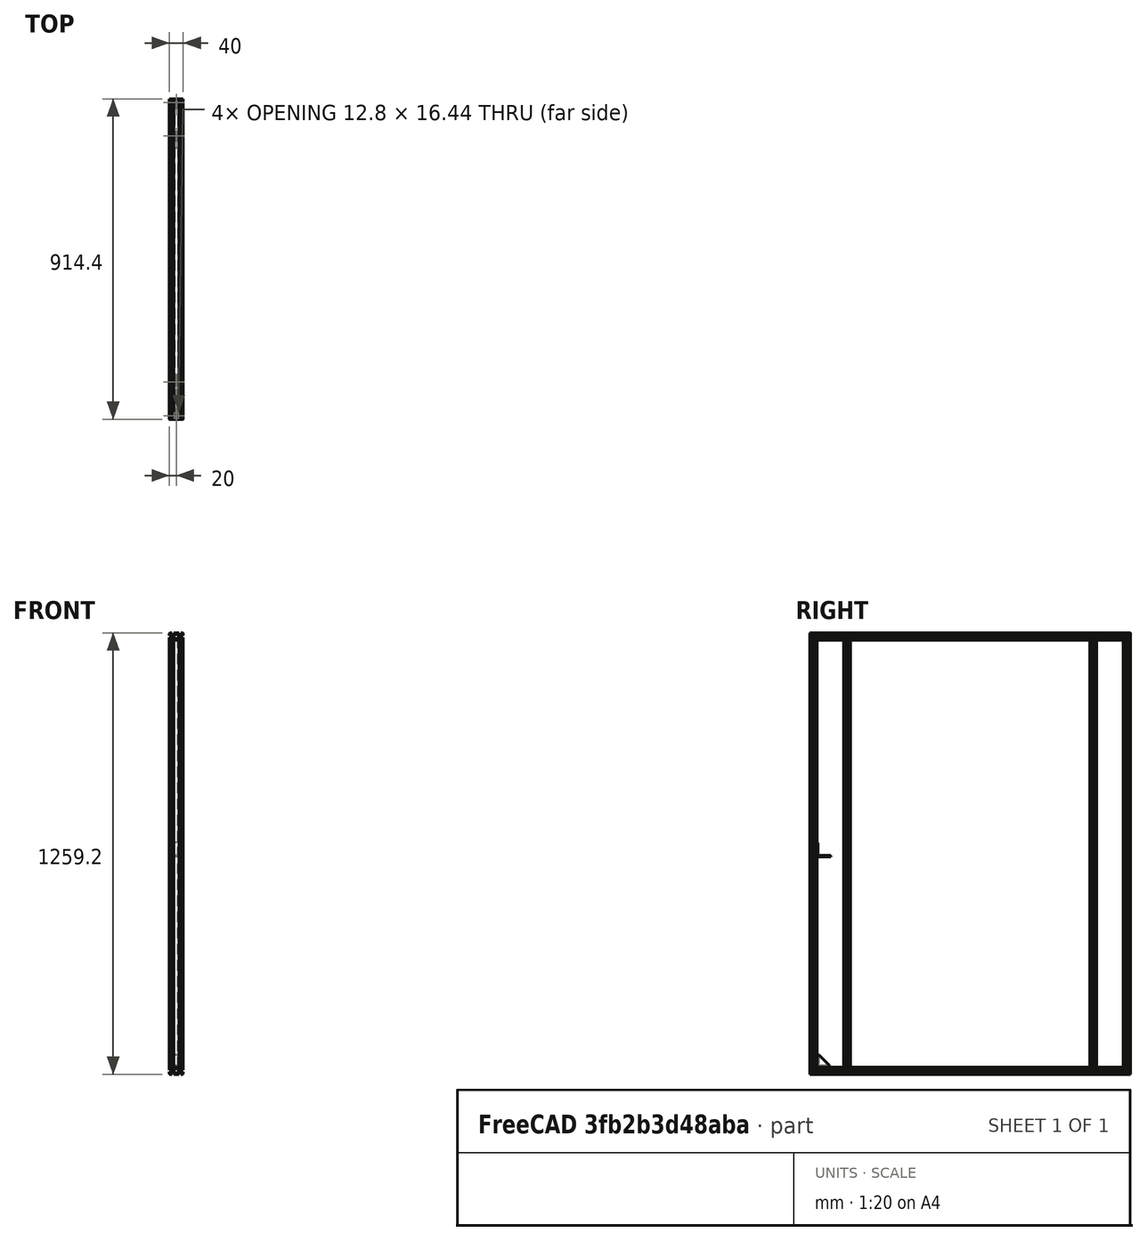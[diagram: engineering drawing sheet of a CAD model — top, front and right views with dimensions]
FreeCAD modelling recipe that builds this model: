
FCSTD DOCUMENT  (FreeCAD 0.19R)
Label: design
License: All rights reserved
LicenseURL: http://en.wikipedia.org/wiki/All_rights_reserved
objects: App::FeaturePython×54, Part::FeaturePython×34, Part::Feature×8
note: 41 computed .brp shape members not serialized (recipe doc carries the construction recipe); baked Part::Feature solids carry a one-line shape summary decoded from their .brp

FEATURE [Part::Feature] Part__Feature  label="Left Side Inner 5537T16_T-Slotted Framing"
  Placement = pos=(468.64,437.451,18.9991) rot=(0,0,1;0rad)
  shape: bbox 40 x 20 x 1219 mm, 102 faces (baked)
FEATURE [Part::Feature] Part__Feature001  label="Left Side Outer 5537T16_T-Slotted Framing"
  Placement = pos=(468.64,533.651,18.9991) rot=(0,0,1;0rad)
  shape: bbox 40 x 20 x 1219 mm, 102 faces (baked)
FEATURE [Part::Feature] Part__Feature002  label="Right Side Inner 5537T16_T-Slotted Framing"
  Placement = pos=(468.64,-264.549,18.9991) rot=(0,0,1;0rad)
  shape: bbox 40 x 20 x 1219 mm, 102 faces (baked)
FEATURE [Part::Feature] Part__Feature003  label="Right Side Outer 5537T16_T-Slotted Framing"
  Placement = pos=(468.64,-360.749,18.9991) rot=(0,0,1;0rad)
  shape: bbox 40 x 20 x 1219 mm, 102 faces (baked)
FEATURE [Part::Feature] Part__Feature004  label="Top Side 5537T706_T-Slotted Framing"
  Placement = pos=(468.64,86.451,638.599) rot=(1,0,0;1.5708rad)
  shape: bbox 40 x 914.4 x 20 mm, 102 faces (baked)
FEATURE [Part::Feature] Part__Feature005  label="Bottom Side 5537T706_T-Slotted Framing"
  Placement = pos=(468.64,86.451,-600.601) rot=(-1,0,0;4.71239rad)
  shape: bbox 40 x 914.4 x 20 mm, 102 faces (baked)
FEATURE [Part::Feature] Solid  label="5537T442_T-Slotted Framing"
  Placement = pos=(467.64,-350.749,10.5111) rot=(0.57735,0.57735,0.57735;2.0944rad)
  shape: bbox 38 x 40 x 40 mm, 25 faces (baked)
FEATURE [Part::Feature] Solid001  label="5537T197_T-Slotted Framing"
  Placement = pos=(467.64,-350.749,-590.601) rot=(0,-1,0;1.5708rad)
  shape: bbox 38 x 38 x 38 mm, 67 faces (baked)
FEATURE [Part::FeaturePython] Parts  # WARN: FeaturePython — macro-defined, semantics opaque (R4)
  Group = -> [Part__Feature004,Part__Feature,Part__Feature001,Part__Feature002,Part__Feature003,Part__Feature005,Solid,Solid001]
  GroupMode = 0
FEATURE [Part::FeaturePython] Assembly  # WARN: FeaturePython — macro-defined, semantics opaque (R4)
  AutoRelax = true
  BuildShape = 0
  Freeze = false
  Group = -> [Constraints,Elements,Parts]
  Verbose = false
  _SolverType = 1
  _Version = 1
FEATURE [App::FeaturePython] Constraints  # WARN: FeaturePython — macro-defined, semantics opaque (R4)
  Group = -> [Constraint,Constraint001,Constraint002,Constraint003,Constraint004,Constraint007,Constraint008,Constraint009,Constraint010,Constraint011,Constraint012,Constraint013,Constraint014,Constraint015,Constraint016,Constraint017]
  _Version = 1
FEATURE [App::FeaturePython] Elements  # WARN: FeaturePython — macro-defined, semantics opaque (R4)
  Group = -> [_Element,_Element001,_Element002,_Element003,_Element004,_Element005,_Element006,_Element007,_Element008,_Element009,_Element010,_Element011,_Element012,_Element013,_Element014,_Element015,_Element016,_Element017,_Element018,_Element019,_Element020,_Element021,_Element022,_Element023,_Element024,_Element025,_Element028,_Element029,_Element030,_Element031,_Element032,_Element033]
FEATURE [App::FeaturePython] Constraint  label="Side_End_Alignment"  # WARN: FeaturePython — macro-defined, semantics opaque (R4)
  Angle = 0
  AnglePitch = 0
  AngleRoll = 0
  Cascade = false
  Disabled = false
  Group = -> [ElementLink,ElementLink001,ElementLink002,ElementLink003]
  LockAngle = false
  _ConstraintType = 37
  _Parent = -> Constraints
FEATURE [App::FeaturePython] ElementLink  label="_Element"  # link proxy (typed FeaturePython)
  LinkTransform = true
  LinkedObject = -> _Element
  _Parent = -> Constraint
FEATURE [Part::FeaturePython] _Element  # link proxy (typed FeaturePython)
  Detach = false
  LinkTransform = true
  LinkedObject = -> Part__Feature003 [Face20]
  _Parent = -> Elements
FEATURE [App::FeaturePython] ElementLink001  label="_Element001"  # link proxy (typed FeaturePython)
  LinkTransform = true
  LinkedObject = -> _Element001
  _Parent = -> Constraint
FEATURE [Part::FeaturePython] _Element001  # link proxy (typed FeaturePython)
  Detach = false
  LinkTransform = true
  LinkedObject = -> Part__Feature002 [Face20]
  _Parent = -> Elements
FEATURE [App::FeaturePython] ElementLink002  label="_Element002"  # link proxy (typed FeaturePython)
  LinkTransform = true
  LinkedObject = -> _Element002
  _Parent = -> Constraint
FEATURE [Part::FeaturePython] _Element002  # link proxy (typed FeaturePython)
  Detach = false
  LinkTransform = true
  LinkedObject = -> Part__Feature [Face20]
  _Parent = -> Elements
FEATURE [App::FeaturePython] ElementLink003  label="_Element003"  # link proxy (typed FeaturePython)
  LinkTransform = true
  LinkedObject = -> _Element003
  _Parent = -> Constraint
FEATURE [Part::FeaturePython] _Element003  # link proxy (typed FeaturePython)
  Detach = false
  LinkTransform = true
  LinkedObject = -> Part__Feature001 [Face20]
  _Parent = -> Elements
FEATURE [App::FeaturePython] Constraint001  label="Side_Top_Alignment"  # WARN: FeaturePython — macro-defined, semantics opaque (R4)
  Angle = 0
  AnglePitch = 0
  AngleRoll = 0
  Cascade = false
  Disabled = false
  Group = -> [ElementLink004,ElementLink005,ElementLink006,ElementLink007]
  LockAngle = false
  _ConstraintType = 37
  _Parent = -> Constraints
FEATURE [App::FeaturePython] ElementLink004  label="_Element004"  # link proxy (typed FeaturePython)
  LinkTransform = true
  LinkedObject = -> _Element004
  _Parent = -> Constraint001
FEATURE [Part::FeaturePython] _Element004  # link proxy (typed FeaturePython)
  Detach = false
  LinkTransform = true
  LinkedObject = -> Part__Feature003 [Face28]
  _Parent = -> Elements
FEATURE [App::FeaturePython] ElementLink005  label="_Element005"  # link proxy (typed FeaturePython)
  LinkTransform = true
  LinkedObject = -> _Element005
  _Parent = -> Constraint001
FEATURE [Part::FeaturePython] _Element005  # link proxy (typed FeaturePython)
  Detach = false
  LinkTransform = true
  LinkedObject = -> Part__Feature002 [Face28]
  _Parent = -> Elements
FEATURE [App::FeaturePython] ElementLink006  label="_Element006"  # link proxy (typed FeaturePython)
  LinkTransform = true
  LinkedObject = -> _Element006
  _Parent = -> Constraint001
FEATURE [Part::FeaturePython] _Element006  # link proxy (typed FeaturePython)
  Detach = false
  LinkTransform = true
  LinkedObject = -> Part__Feature [Face28]
  _Parent = -> Elements
FEATURE [App::FeaturePython] ElementLink007  label="_Element007"  # link proxy (typed FeaturePython)
  LinkTransform = true
  LinkedObject = -> _Element007
  _Parent = -> Constraint001
FEATURE [Part::FeaturePython] _Element007  # link proxy (typed FeaturePython)
  Detach = false
  LinkTransform = true
  LinkedObject = -> Part__Feature001 [Face28]
  _Parent = -> Elements
FEATURE [Part::FeaturePython] _Element008  # link proxy (typed FeaturePython)
  Detach = false
  LinkTransform = true
  LinkedObject = -> Part__Feature004 [Face19]
  _Parent = -> Elements
FEATURE [Part::FeaturePython] _Element009  # link proxy (typed FeaturePython)
  Detach = false
  LinkTransform = true
  LinkedObject = -> Part__Feature005 [Face19]
  _Parent = -> Elements
FEATURE [Part::FeaturePython] _Element010  # link proxy (typed FeaturePython)
  Detach = false
  LinkTransform = true
  LinkedObject = -> Part__Feature005 [Face60]
  _Parent = -> Elements
FEATURE [Part::FeaturePython] _Element011  # link proxy (typed FeaturePython)
  Detach = false
  LinkTransform = true
  LinkedObject = -> Part__Feature004 [Face60]
  _Parent = -> Elements
FEATURE [App::FeaturePython] Constraint002  label="PlaneAlignment"  # WARN: FeaturePython — macro-defined, semantics opaque (R4)
  Angle = 0
  AnglePitch = 0
  AngleRoll = 0
  Cascade = false
  Disabled = false
  Group = -> [ElementLink008,ElementLink009]
  LockAngle = false
  _ConstraintType = 37
  _Parent = -> Constraints
FEATURE [App::FeaturePython] ElementLink008  label="_Element012"  # link proxy (typed FeaturePython)
  LinkTransform = true
  LinkedObject = -> _Element012
  _Parent = -> Constraint002
FEATURE [Part::FeaturePython] _Element012  # link proxy (typed FeaturePython)
  Detach = false
  LinkTransform = true
  LinkedObject = -> Part__Feature005 [Face55]
  _Parent = -> Elements
FEATURE [App::FeaturePython] ElementLink009  label="_Element"  # link proxy (typed FeaturePython)
  LinkTransform = true
  LinkedObject = -> _Element
  _Parent = -> Constraint002
FEATURE [App::FeaturePython] Constraint003  label="PlaneAlignment001"  # WARN: FeaturePython — macro-defined, semantics opaque (R4)
  Angle = 0
  AnglePitch = 0
  AngleRoll = 0
  Cascade = false
  Disabled = false
  Group = -> [ElementLink010,ElementLink011]
  LockAngle = false
  _ConstraintType = 37
  _Parent = -> Constraints
FEATURE [App::FeaturePython] ElementLink010  label="_Element013"  # link proxy (typed FeaturePython)
  LinkTransform = true
  LinkedObject = -> _Element013
  _Parent = -> Constraint003
FEATURE [Part::FeaturePython] _Element013  # link proxy (typed FeaturePython)
  Detach = false
  LinkTransform = true
  LinkedObject = -> Part__Feature003 [Face23]
  _Parent = -> Elements
FEATURE [App::FeaturePython] ElementLink011  label="_Element009"  # link proxy (typed FeaturePython)
  LinkTransform = true
  LinkedObject = -> _Element009
  _Parent = -> Constraint003
FEATURE [App::FeaturePython] Constraint004  label="PlaneAlignment002"  # WARN: FeaturePython — macro-defined, semantics opaque (R4)
  Angle = 0
  AnglePitch = 0
  AngleRoll = 0
  Cascade = false
  Disabled = false
  Group = -> [ElementLink012,ElementLink013]
  LockAngle = false
  _ConstraintType = 37
  _Parent = -> Constraints
FEATURE [App::FeaturePython] ElementLink012  label="_Element014"  # link proxy (typed FeaturePython)
  LinkTransform = true
  LinkedObject = -> _Element014
  _Parent = -> Constraint004
FEATURE [Part::FeaturePython] _Element014  # link proxy (typed FeaturePython)
  Detach = false
  LinkTransform = true
  LinkedObject = -> Part__Feature003 [Face8]
  _Parent = -> Elements
FEATURE [App::FeaturePython] ElementLink013  label="_Element015"  # link proxy (typed FeaturePython)
  LinkTransform = true
  LinkedObject = -> _Element015
  _Parent = -> Constraint004
FEATURE [Part::FeaturePython] _Element015  # link proxy (typed FeaturePython)
  Detach = false
  LinkTransform = true
  LinkedObject = -> Part__Feature005 [Face45]
  _Parent = -> Elements
FEATURE [Part::FeaturePython] _Element016  # link proxy (typed FeaturePython)
  Detach = false
  LinkTransform = true
  LinkedObject = -> Part__Feature004 [Face55]
  _Parent = -> Elements
FEATURE [Part::FeaturePython] _Element017  # link proxy (typed FeaturePython)
  Detach = false
  LinkTransform = true
  LinkedObject = -> Part__Feature003 [Face19]
  _Parent = -> Elements
FEATURE [App::FeaturePython] Constraint007  label="PlaneAlignment005"  # WARN: FeaturePython — macro-defined, semantics opaque (R4)
  Angle = 0
  AnglePitch = 0
  AngleRoll = 0
  Cascade = false
  Disabled = false
  Group = -> [ElementLink018,ElementLink019]
  LockAngle = false
  _ConstraintType = 37
  _Parent = -> Constraints
FEATURE [App::FeaturePython] ElementLink018  label="_Element008"  # link proxy (typed FeaturePython)
  LinkTransform = true
  LinkedObject = -> _Element008
  _Parent = -> Constraint007
FEATURE [App::FeaturePython] ElementLink019  label="_Element009"  # link proxy (typed FeaturePython)
  LinkTransform = true
  LinkedObject = -> _Element009
  _Parent = -> Constraint007
FEATURE [App::FeaturePython] Constraint008  label="PlaneAlignment006"  # WARN: FeaturePython — macro-defined, semantics opaque (R4)
  Angle = 0
  AnglePitch = 0
  AngleRoll = 0
  Cascade = false
  Disabled = false
  Group = -> [ElementLink020,ElementLink021]
  LockAngle = false
  _ConstraintType = 37
  _Parent = -> Constraints
FEATURE [App::FeaturePython] ElementLink020  label="_Element014"  # link proxy (typed FeaturePython)
  LinkTransform = true
  LinkedObject = -> _Element014
  _Parent = -> Constraint008
FEATURE [App::FeaturePython] ElementLink021  label="_Element018"  # link proxy (typed FeaturePython)
  LinkTransform = true
  LinkedObject = -> _Element018
  _Parent = -> Constraint008
FEATURE [Part::FeaturePython] _Element018  # link proxy (typed FeaturePython)
  Detach = false
  LinkTransform = true
  LinkedObject = -> Part__Feature004 [Face8]
  _Parent = -> Elements
FEATURE [App::FeaturePython] Constraint009  label="PlaneAlignment007"  # WARN: FeaturePython — macro-defined, semantics opaque (R4)
  Angle = 0
  AnglePitch = 0
  AngleRoll = 0
  Cascade = false
  Disabled = false
  Group = -> [ElementLink022,ElementLink023]
  LockAngle = false
  _ConstraintType = 37
  _Parent = -> Constraints
FEATURE [App::FeaturePython] ElementLink022  label="_Element019"  # link proxy (typed FeaturePython)
  LinkTransform = true
  LinkedObject = -> _Element019
  _Parent = -> Constraint009
FEATURE [Part::FeaturePython] _Element019  # link proxy (typed FeaturePython)
  Detach = false
  LinkTransform = true
  LinkedObject = -> Part__Feature004 [Face23]
  _Parent = -> Elements
FEATURE [App::FeaturePython] ElementLink023  label="_Element017"  # link proxy (typed FeaturePython)
  LinkTransform = true
  LinkedObject = -> _Element017
  _Parent = -> Constraint009
FEATURE [App::FeaturePython] Constraint010  label="PlaneAlignment008"  # WARN: FeaturePython — macro-defined, semantics opaque (R4)
  Angle = 0
  AnglePitch = 0
  AngleRoll = 0
  Cascade = false
  Disabled = false
  Group = -> [ElementLink024,ElementLink025]
  LockAngle = false
  _ConstraintType = 37
  _Parent = -> Constraints
FEATURE [App::FeaturePython] ElementLink024  label="_Element020"  # link proxy (typed FeaturePython)
  LinkTransform = true
  LinkedObject = -> _Element020
  _Parent = -> Constraint010
FEATURE [Part::FeaturePython] _Element020  # link proxy (typed FeaturePython)
  Detach = false
  LinkTransform = true
  LinkedObject = -> Part__Feature001 [Face55]
  _Parent = -> Elements
FEATURE [App::FeaturePython] ElementLink025  label="_Element021"  # link proxy (typed FeaturePython)
  LinkTransform = true
  LinkedObject = -> _Element021
  _Parent = -> Constraint010
FEATURE [Part::FeaturePython] _Element021  # link proxy (typed FeaturePython)
  Detach = false
  LinkTransform = true
  LinkedObject = -> Part__Feature004 [Face20]
  _Parent = -> Elements
FEATURE [Part::FeaturePython] _Element022  # link proxy (typed FeaturePython)
  Detach = false
  LinkTransform = true
  LinkedObject = -> Part__Feature002 [Face23]
  _Parent = -> Elements
FEATURE [Part::FeaturePython] _Element023  # link proxy (typed FeaturePython)
  Detach = false
  LinkTransform = true
  LinkedObject = -> Part__Feature003 [Face55]
  _Parent = -> Elements
FEATURE [App::FeaturePython] Constraint011  label="PointsPlaneDistance"  # WARN: FeaturePython — macro-defined, semantics opaque (R4)
  Disabled = false
  Distance = -76.2
  Group = -> [ElementLink026,ElementLink027]
  _ConstraintType = 7
  _Parent = -> Constraints
FEATURE [App::FeaturePython] ElementLink026  label="_Element023"  # link proxy (typed FeaturePython)
  LinkTransform = true
  LinkedObject = -> _Element023
  _Parent = -> Constraint011
FEATURE [App::FeaturePython] ElementLink027  label="_Element022"  # link proxy (typed FeaturePython)
  LinkTransform = true
  LinkedObject = -> _Element022
  _Parent = -> Constraint011
FEATURE [App::FeaturePython] Constraint012  label="PointsPlaneDistance001"  # WARN: FeaturePython — macro-defined, semantics opaque (R4)
  Disabled = false
  Distance = -76.2
  Group = -> [ElementLink028,ElementLink029]
  _ConstraintType = 7
  _Parent = -> Constraints
FEATURE [App::FeaturePython] ElementLink028  label="_Element024"  # link proxy (typed FeaturePython)
  LinkTransform = true
  LinkedObject = -> _Element024
  _Parent = -> Constraint012
FEATURE [Part::FeaturePython] _Element024  # link proxy (typed FeaturePython)
  Detach = false
  LinkTransform = true
  LinkedObject = -> Part__Feature001 [Face23]
  _Parent = -> Elements
FEATURE [App::FeaturePython] ElementLink029  label="_Element025"  # link proxy (typed FeaturePython)
  LinkTransform = true
  LinkedObject = -> _Element025
  _Parent = -> Constraint012
FEATURE [Part::FeaturePython] _Element025  # link proxy (typed FeaturePython)
  Detach = false
  LinkTransform = true
  LinkedObject = -> Part__Feature [Face55]
  _Parent = -> Elements
FEATURE [Part::FeaturePython] _Element028  # link proxy (typed FeaturePython)
  Detach = false
  LinkTransform = true
  LinkedObject = -> Part__Feature003 [Face60]
  _Parent = -> Elements
FEATURE [App::FeaturePython] Constraint013  label="PlaneAlignment009"  # WARN: FeaturePython — macro-defined, semantics opaque (R4)
  Angle = 0
  AnglePitch = 0
  AngleRoll = 0
  Cascade = false
  Disabled = false
  Group = -> [ElementLink030,ElementLink031]
  LockAngle = false
  _ConstraintType = 37
  _Parent = -> Constraints
FEATURE [App::FeaturePython] ElementLink030  label="_Element029"  # link proxy (typed FeaturePython)
  LinkTransform = true
  LinkedObject = -> _Element029
  _Parent = -> Constraint013
FEATURE [Part::FeaturePython] _Element029  # link proxy (typed FeaturePython)
  Detach = false
  LinkTransform = true
  LinkedObject = -> Solid [Face10]
  _Parent = -> Elements
FEATURE [App::FeaturePython] ElementLink031  label="_Element023"  # link proxy (typed FeaturePython)
  LinkTransform = true
  LinkedObject = -> _Element023
  _Parent = -> Constraint013
FEATURE [App::FeaturePython] Constraint014  label="PlaneAlignment010"  # WARN: FeaturePython — macro-defined, semantics opaque (R4)
  Angle = 0
  AnglePitch = 0
  AngleRoll = 0
  Cascade = false
  Disabled = false
  Group = -> [ElementLink032,ElementLink033]
  LockAngle = false
  _ConstraintType = 37
  _Parent = -> Constraints
FEATURE [App::FeaturePython] ElementLink032  label="_Element030"  # link proxy (typed FeaturePython)
  LinkTransform = true
  LinkedObject = -> _Element030
  _Parent = -> Constraint014
FEATURE [Part::FeaturePython] _Element030  # link proxy (typed FeaturePython)
  Detach = false
  LinkTransform = true
  LinkedObject = -> Solid [Face17]
  _Parent = -> Elements
FEATURE [App::FeaturePython] ElementLink033  label="_Element028"  # link proxy (typed FeaturePython)
  LinkTransform = true
  LinkedObject = -> _Element028
  _Parent = -> Constraint014
FEATURE [App::FeaturePython] Constraint015  label="PlaneAlignment011"  # WARN: FeaturePython — macro-defined, semantics opaque (R4)
  Angle = 0
  AnglePitch = 0
  AngleRoll = 0
  Cascade = false
  Disabled = false
  Group = -> [ElementLink034,ElementLink035]
  LockAngle = false
  _ConstraintType = 37
  _Parent = -> Constraints
FEATURE [App::FeaturePython] ElementLink034  label="_Element031"  # link proxy (typed FeaturePython)
  LinkTransform = true
  LinkedObject = -> _Element031
  _Parent = -> Constraint015
FEATURE [Part::FeaturePython] _Element031  # link proxy (typed FeaturePython)
  Detach = false
  LinkTransform = true
  LinkedObject = -> Solid001 [Face2]
  _Parent = -> Elements
FEATURE [App::FeaturePython] ElementLink035  label="_Element023"  # link proxy (typed FeaturePython)
  LinkTransform = true
  LinkedObject = -> _Element023
  _Parent = -> Constraint015
FEATURE [App::FeaturePython] Constraint016  label="PlaneAlignment012"  # WARN: FeaturePython — macro-defined, semantics opaque (R4)
  Angle = 0
  AnglePitch = 0
  AngleRoll = 0
  Cascade = false
  Disabled = false
  Group = -> [ElementLink036,ElementLink037]
  LockAngle = false
  _ConstraintType = 37
  _Parent = -> Constraints
FEATURE [App::FeaturePython] ElementLink036  label="_Element032"  # link proxy (typed FeaturePython)
  LinkTransform = true
  LinkedObject = -> _Element032
  _Parent = -> Constraint016
FEATURE [Part::FeaturePython] _Element032  # link proxy (typed FeaturePython)
  Detach = false
  LinkTransform = true
  LinkedObject = -> Solid001 [Face8]
  _Parent = -> Elements
FEATURE [App::FeaturePython] ElementLink037  label="_Element028"  # link proxy (typed FeaturePython)
  LinkTransform = true
  LinkedObject = -> _Element028
  _Parent = -> Constraint016
FEATURE [App::FeaturePython] Constraint017  label="PlaneAlignment013"  # WARN: FeaturePython — macro-defined, semantics opaque (R4)
  Angle = 0
  AnglePitch = 0
  AngleRoll = 0
  Cascade = false
  Disabled = false
  Group = -> [ElementLink038,ElementLink039]
  LockAngle = false
  _ConstraintType = 37
  _Parent = -> Constraints
FEATURE [App::FeaturePython] ElementLink038  label="_Element033"  # link proxy (typed FeaturePython)
  LinkTransform = true
  LinkedObject = -> _Element033
  _Parent = -> Constraint017
FEATURE [Part::FeaturePython] _Element033  # link proxy (typed FeaturePython)
  Detach = false
  LinkTransform = true
  LinkedObject = -> Solid001 [Face1]
  _Parent = -> Elements
FEATURE [App::FeaturePython] ElementLink039  label="_Element012"  # link proxy (typed FeaturePython)
  LinkTransform = true
  LinkedObject = -> _Element012
  _Parent = -> Constraint017
